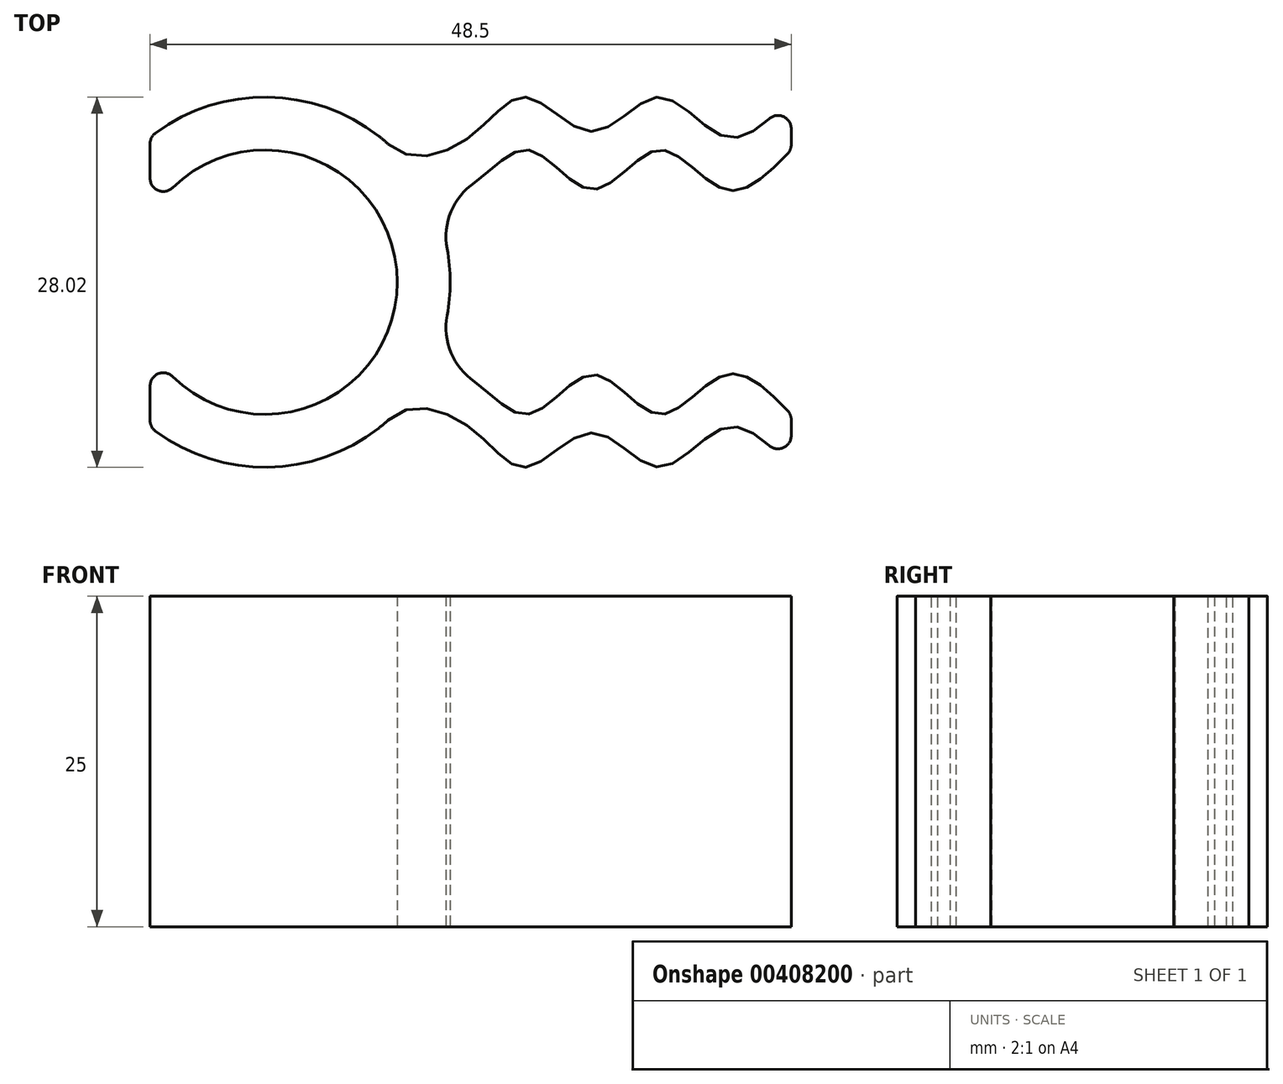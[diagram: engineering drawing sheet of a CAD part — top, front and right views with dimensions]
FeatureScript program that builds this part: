
annotation { "Feature Type Name" : "Feature", "Feature Type Description" : "" }
export const myFeature = defineFeature(function(context is Context, id is Id, definition is map)
    precondition{}
    {
        {
            var Q0;
            Q0=qCreatedBy(makeId("Top.planeOp"),FACE);
            var sketch = newSketch(context, id + "F0", { "sketchPlane" : qUnion([Q0])});
            skLineSegment(sketch, "E0", {"start": v(-8.7, 51.6) * mm, "end": v(-8.7, 10.97) * mm, "construction": true});
            skLineSegment(sketch, "E1", {"start": v(-8.7, -10.97) * mm, "end": v(-8.7, -60.12) * mm, "construction": true});
            skArc(sketch, "E2", {"start": v(-8.7, -10.97) * mm, "mid": v(0.3, -14) * mm, "end": v(9.15, -10.6) * mm});
            skLineSegment(sketch, "E3", {"start": v(-8.7, 5.88) * mm, "end": v(-8.7, 4.93) * mm});
            skLineSegment(sketch, "E4", {"start": v(-8.7, -5.88) * mm, "end": v(-8.7, -10.97) * mm});
            skArc(sketch, "E5", {"start": v(-8.7, -4.93) * mm, "mid": v(10, 0) * mm, "end": v(-8.7, 4.93) * mm});
            skLineSegment(sketch, "E6", {"start": v(-8.7, 10.97) * mm, "end": v(-8.7, 5.88) * mm});
            skLineSegment(sketch, "E7", {"start": v(-46.8, 7) * mm, "end": v(52, 7) * mm, "construction": true});
            skLineSegment(sketch, "E8", {"start": v(-47.4, 10) * mm, "end": v(54.57, 10) * mm, "construction": true});
            skPoint(sketch, "E9", {"position": v(9.8, 10) * mm});
            skPoint(sketch, "E10", {"position": v(19.8, 10) * mm});
            skPoint(sketch, "E11", {"position": v(14.8, 7) * mm});
            skLineSegment(sketch, "E12", {"start": v(19.8, 10) * mm, "end": v(19.8, 7) * mm, "construction": true});
            skPoint(sketch, "E13.1.0.0", {"position": v(29.8, 10) * mm});
            skPoint(sketch, "E13.2.0.0", {"position": v(39.8, 10) * mm});
            skLineSegment(sketch, "E13.direction1", {"start": v(19.8, 10) * mm, "end": v(29.8, 10) * mm, "construction": true});
            skPoint(sketch, "E14.1.0.0", {"position": v(24.8, 7) * mm});
            skPoint(sketch, "E14.2.0.0", {"position": v(34.8, 7) * mm});
            skLineSegment(sketch, "E14.direction1", {"start": v(14.8, 7) * mm, "end": v(24.8, 7) * mm, "construction": true});
            skFitSpline(sketch, "E15", {"points": [v(9.8, 10) * mm, v(14.8, 7) * mm, v(19.8, 10) * mm, v(24.8, 7) * mm, v(29.8, 10) * mm, v(34.8, 7) * mm, v(39.8, 10) * mm], "startDerivative": vector(30, -31.15) * mm, "endDerivative": vector(30, 31.15) * mm});
            skFitSpline(sketch, "E16", {"points": [v(9.15, 10.6) * mm, v(15.5, 11) * mm, v(19.8, 14) * mm, v(24.8, 11.4) * mm, v(29.8, 14) * mm, v(34.8, 11) * mm, v(39.8, 14) * mm], "startDerivative": vector(30, -31.15) * mm, "endDerivative": vector(30, 31.15) * mm});
            skLineSegment(sketch, "E17", {"start": v(39.8, 14) * mm, "end": v(39.8, 10) * mm});
            skFitSpline(sketch, "E18.MirrorCS", {"points": [v(9.8, -10) * mm, v(14.8, -7) * mm, v(19.8, -10) * mm, v(24.8, -7) * mm, v(29.8, -10) * mm, v(34.8, -7) * mm, v(39.8, -10) * mm], "startDerivative": vector(30, 31.15) * mm, "endDerivative": vector(30, -31.15) * mm});
            skFitSpline(sketch, "E19.MirrorCS", {"points": [v(9.15, -10.6) * mm, v(15.5, -11) * mm, v(19.8, -14) * mm, v(24.8, -11.4) * mm, v(29.8, -14) * mm, v(34.8, -11) * mm, v(39.8, -14) * mm], "startDerivative": vector(30, 31.15) * mm, "endDerivative": vector(30, -31.15) * mm});
            skLineSegment(sketch, "E20.MirrorCS", {"start": v(9.15, -10.6) * mm, "end": v(9.15, -10.6) * mm});
            skLineSegment(sketch, "E21.MirrorCS", {"start": v(39.8, -14) * mm, "end": v(39.8, -10) * mm});
            skArc(sketch, "E22.trimOffspring", {"start": v(9.15, 10.6) * mm, "mid": v(0.3, 14) * mm, "end": v(-8.7, 10.97) * mm});
            skArc(sketch, "E23.trimOffspring", {"start": v(13.77, -2.52) * mm, "mid": v(14, 0) * mm, "end": v(13.77, 2.52) * mm});
            skArc(sketch, "E24.filletArc", {"start": v(13.77, -2.52) * mm, "mid": v(14.07, -5.33) * mm, "end": v(15.84, -7.53) * mm});
            skArc(sketch, "E25.filletArc", {"start": v(15.84, 7.53) * mm, "mid": v(14.07, 5.33) * mm, "end": v(13.77, 2.52) * mm});
            skLineSegment(sketch, "E26", {"start": v(34.8, 7) * mm, "end": v(34.8, 15.15) * mm, "construction": true});
            skLineSegment(sketch, "E27", {"start": v(24.8, 7) * mm, "end": v(24.8, 15.79) * mm, "construction": true});
            skPoint(sketch, "E27.endSnap0", {"position": v(24.8, 10) * mm});
            skLineSegment(sketch, "E28", {"start": v(19.8, 7) * mm, "end": v(19.8, 21) * mm, "construction": true});
            skLineSegment(sketch, "E29", {"start": v(29.8, 10) * mm, "end": v(29.8, 18) * mm, "construction": true});
            skLineSegment(sketch, "E30.trimOffspring", {"start": v(-8.7, -4.93) * mm, "end": v(-8.7, -5.88) * mm});
            skSolve(sketch);
        }
        {
            var Q0;
            Q0=makeQuery(id+"F0.imprint","IMPRINT",FACE,{"disambiguationData":[TD([[makeQuery(id+"F0.imprint","IMPRINT",EDGE,{"derivedFrom":sQuery(id+"F0.wireOp",EDGE,"E2")}),1.0]])]});
            extrude(context, id + "F1", {"entities" : qUnion([Q0]), "flatOperationType" : FlatOperationType.REMOVE, "offsetDistance" : 25 * mm, "depth" : 25 * mm, "domain" : OperationDomain.MODEL});
        }
        {
            var Q0;
            Q0=makeQuery(id+"F1.opExtrude","SWEPT_EDGE",EDGE,{"disambiguationData":[OSD([sQuery(id+"F0.wireOp",EDGE,"E4"),sQuery(id+"F0.wireOp",EDGE,"E5")])]});
            var Q1;
            Q1=makeQuery(id+"F1.opExtrude","SWEPT_EDGE",EDGE,{"disambiguationData":[OSD([sQuery(id+"F0.wireOp",EDGE,"E5"),sQuery(id+"F0.wireOp",EDGE,"E6")])]});
            var Q2;
            Q2=makeQuery(id+"F1.opExtrude","SWEPT_EDGE",EDGE,{"disambiguationData":[OSD([sQuery(id+"F0.wireOp",EDGE,"E2"),sQuery(id+"F0.wireOp",EDGE,"E4")])]});
            var Q3;
            Q3=makeQuery(id+"F1.opExtrude","SWEPT_EDGE",EDGE,{"disambiguationData":[OSD([sQuery(id+"F0.wireOp",EDGE,"E6"),sQuery(id+"F0.wireOp",EDGE,"E22.trimOffspring")])]});
            fillet(context, id + "F2", {"entities" : qUnion([Q0, Q1, Q2, Q3]), "radius" : 1 * mm, "tangentPropagation" : true, "allowEdgeOverflow" : false});
        }
        {
            var Q0;
            Q0=makeQuery(id+"F1.opExtrude","SWEPT_EDGE",EDGE,{"disambiguationData":[OSD([sQuery(id+"F0.wireOp",EDGE,"E19.MirrorCS"),sQuery(id+"F0.wireOp",EDGE,"E21.MirrorCS")])]});
            var Q1;
            Q1=makeQuery(id+"F1.opExtrude","SWEPT_EDGE",EDGE,{"disambiguationData":[OSD([sQuery(id+"F0.wireOp",EDGE,"E18.MirrorCS"),sQuery(id+"F0.wireOp",EDGE,"E21.MirrorCS")])]});
            var Q2;
            Q2=makeQuery(id+"F1.opExtrude","SWEPT_EDGE",EDGE,{"disambiguationData":[OSD([sQuery(id+"F0.wireOp",EDGE,"E15"),sQuery(id+"F0.wireOp",EDGE,"E17")])]});
            var Q3;
            Q3=makeQuery(id+"F1.opExtrude","SWEPT_EDGE",EDGE,{"disambiguationData":[OSD([sQuery(id+"F0.wireOp",EDGE,"E16"),sQuery(id+"F0.wireOp",EDGE,"E17")])]});
            fillet(context, id + "F3", {"entities" : qUnion([Q0, Q1, Q2, Q3]), "radius" : 1 * mm, "tangentPropagation" : true, "allowEdgeOverflow" : false});
        }
        {
            var Q0;
            Q0=makeQuery(id+"F1.opExtrude","SWEPT_EDGE",EDGE,{"disambiguationData":[OSD([sQuery(id+"F0.wireOp",EDGE,"E19.MirrorCS"),sQuery(id+"F0.wireOp",EDGE,"E20.MirrorCS")])]});
            var Q1;
            Q1=makeQuery(id+"F1.opExtrude","SWEPT_EDGE",EDGE,{"disambiguationData":[OSD([sQuery(id+"F0.wireOp",EDGE,"E16"),sQuery(id+"F0.wireOp",EDGE,"UhSvavAm-c1ok-YPRm-zS1v-2geVYcu2kQRH")])]});
            fillet(context, id + "F4", {"entities" : qUnion([Q0, Q1]), "radius" : 10 * mm, "tangentPropagation" : true, "allowEdgeOverflow" : false});
        }
    });
